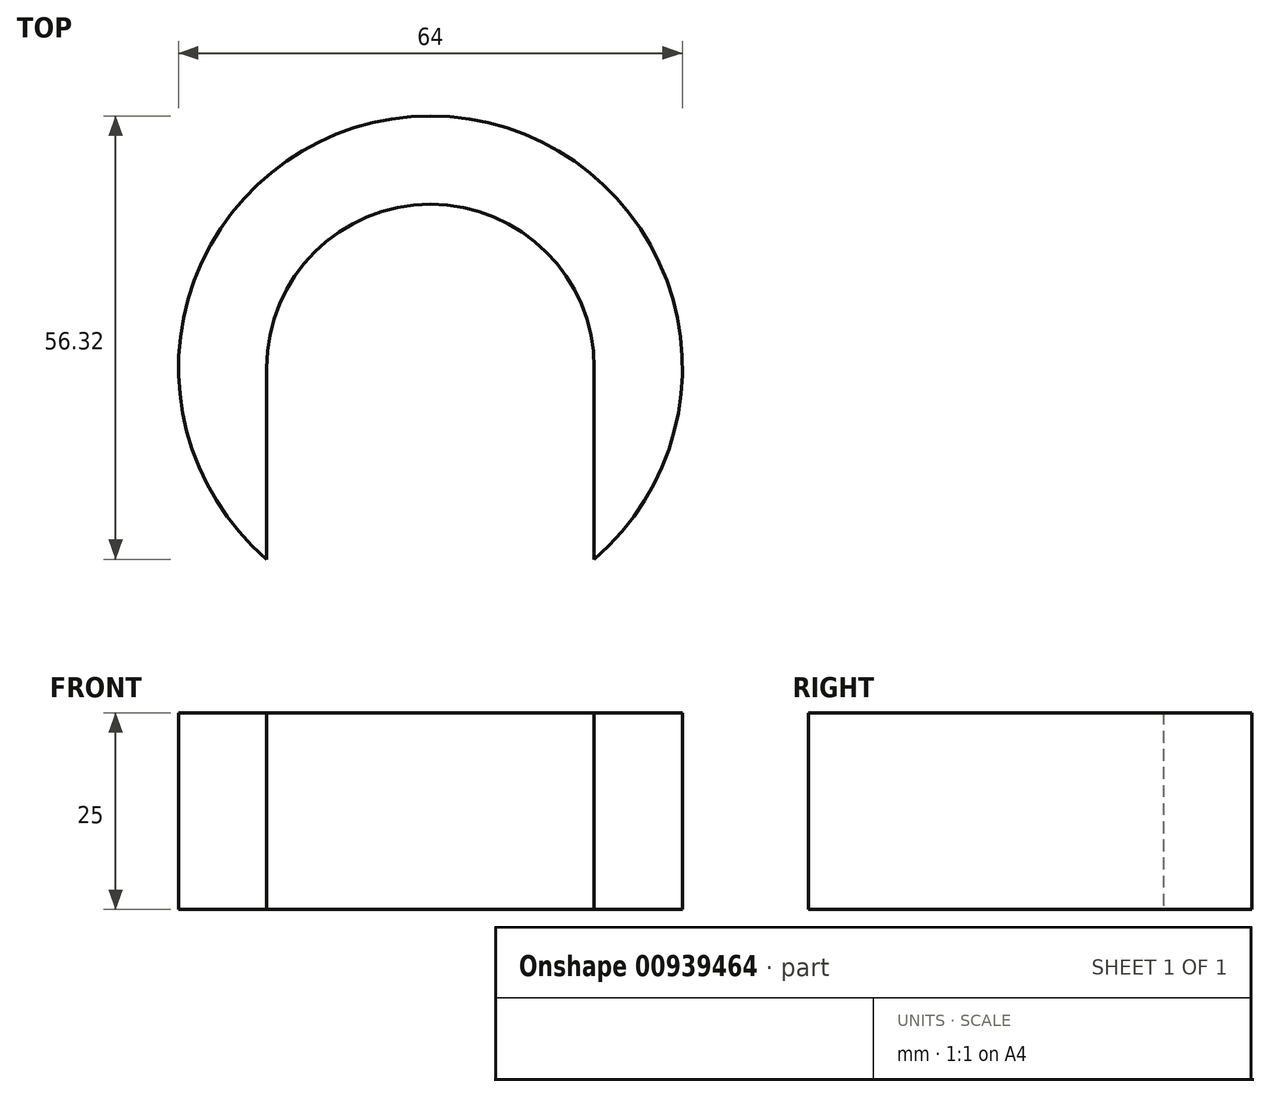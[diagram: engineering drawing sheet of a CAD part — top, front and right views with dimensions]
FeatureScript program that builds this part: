
annotation { "Feature Type Name" : "Feature", "Feature Type Description" : "" }
export const myFeature = defineFeature(function(context is Context, id is Id, definition is map)
    precondition{}
    {
        {
            var Q0;
            Q0=qCreatedBy(makeId("Top.planeOp"),FACE);
            var sketch = newSketch(context, id + "F0", { "sketchPlane" : qUnion([Q0])});
            skArc(sketch, "E0", {"start": v(20.8, 0) * mm, "mid": v(0, 20.8) * mm, "end": v(-20.8, 0) * mm});
            skArc(sketch, "E1", {"start": v(20.8, -24.32) * mm, "mid": v(0, 32) * mm, "end": v(-20.8, -24.32) * mm});
            skLineSegment(sketch, "E2", {"start": v(-20.8, 0) * mm, "end": v(-20.8, -24.32) * mm});
            skLineSegment(sketch, "E3", {"start": v(20.8, 0) * mm, "end": v(20.8, -24.32) * mm});
            skSolve(sketch);
        }
        {
            var Q0;
            Q0=makeQuery(id+"F0.imprint","IMPRINT",FACE,{"disambiguationData":[TD([[makeQuery(id+"F0.imprint","IMPRINT",EDGE,{"derivedFrom":sQuery(id+"F0.wireOp",EDGE,"E0")}),-1.0]])]});
            extrude(context, id + "F1", {"entities" : qUnion([Q0]), "depth" : 25 * mm, "offsetDistance" : 25 * mm});
        }
    });
